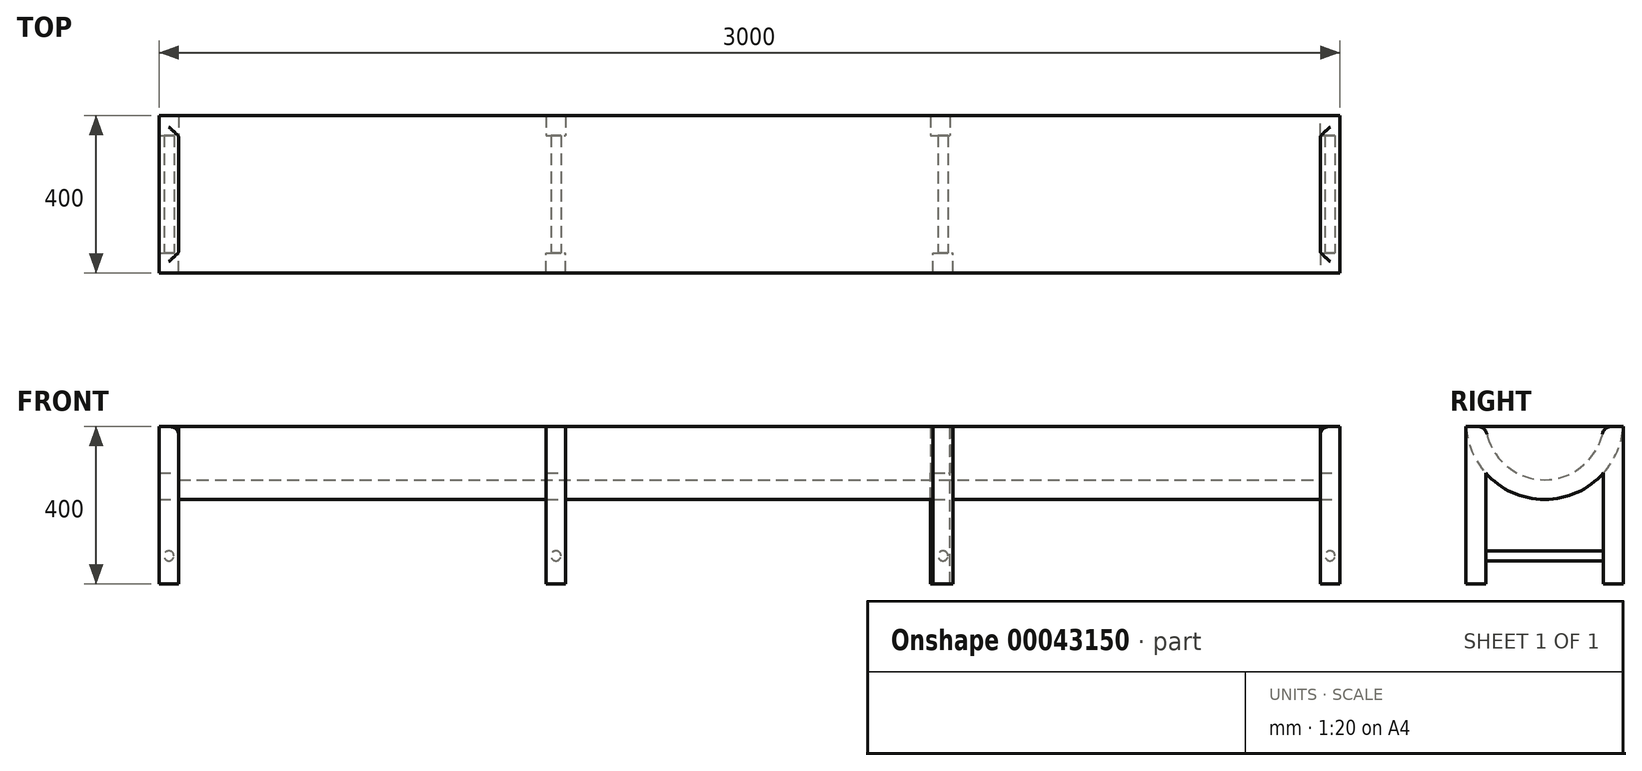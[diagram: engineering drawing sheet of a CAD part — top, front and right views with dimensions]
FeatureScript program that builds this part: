
annotation { "Feature Type Name" : "Feature", "Feature Type Description" : "" }
export const myFeature = defineFeature(function(context is Context, id is Id, definition is map)
    precondition{}
    {
        {
            var Q0;
            Q0=qCreatedBy(makeId("Right.planeOp"),FACE);
            var sketch = newSketch(context, id + "F0", { "sketchPlane" : qUnion([Q0])});
            skArc(sketch, "E0", {"start": v(-199.85, 0) * mm, "mid": v(0.15, -185.28) * mm, "end": v(200.15, 0) * mm});
            skArc(sketch, "E1.0", {"start": v(-149.66, 0) * mm, "mid": v(0.15, -135.28) * mm, "end": v(149.95, 0) * mm});
            skLineSegment(sketch, "E2", {"start": v(-199.85, 0) * mm, "end": v(-149.66, 0) * mm});
            skLineSegment(sketch, "E3", {"start": v(200.15, 0) * mm, "end": v(149.95, 0) * mm});
            skSolve(sketch);
        }
        {
            var Q0;
            Q0=makeQuery(id+"F0.imprint","IMPRINT",FACE,{"disambiguationData":[TD([[makeQuery(id+"F0.imprint","IMPRINT",EDGE,{"derivedFrom":sQuery(id+"F0.wireOp",EDGE,"E0")}),1.0]])]});
            extrude(context, id + "F1", {"entities" : qUnion([Q0]), "endBound" : BoundingType.SYMMETRIC, "oppositeDirection" : true, "depth" : 3000 * mm});
        }
        {
            var Q0;
            Q0=makeQuery(id+"F1.opExtrude","CAP_FACE",FACE,{"disambiguationData":[OSD([sQuery(id+"F0.wireOp",EDGE,"E0"),sQuery(id+"F0.wireOp",EDGE,"E1.0"),sQuery(id+"F0.wireOp",EDGE,"E2"),sQuery(id+"F0.wireOp",EDGE,"E3")])],"isStart":true});
            var sketch = newSketch(context, id + "F2", { "sketchPlane" : qUnion([Q0])});
            skLineSegment(sketch, "E4", {"start": v(-149.66, 0) * mm, "end": v(149.95, 0) * mm});
            skSolve(sketch);
        }
        {
            var Q0;
            Q0=makeQuery(id+"F2.imprint","IMPRINT",FACE,{"disambiguationData":[TD([[makeQuery(id+"F2.imprint","IMPRINT",EDGE,{"derivedFrom":sQuery(id+"F2.wireOp",EDGE,"E4")}),-1.0]])]});
            extrude(context, id + "F3", {"entities" : qUnion([Q0]), "operationType" : NewBodyOperationType.ADD, "oppositeDirection" : true, "depth" : 50 * mm});
        }
        {
            var Q0;
            Q0=makeQuery(id+"F1.opExtrude","CAP_FACE",FACE,{"disambiguationData":[OSD([sQuery(id+"F0.wireOp",EDGE,"E0"),sQuery(id+"F0.wireOp",EDGE,"E1.0"),sQuery(id+"F0.wireOp",EDGE,"E2"),sQuery(id+"F0.wireOp",EDGE,"E3")])],"isStart":false});
            var sketch = newSketch(context, id + "F4", { "sketchPlane" : qUnion([Q0])});
            skLineSegment(sketch, "E5", {"start": v(-149.95, 0) * mm, "end": v(149.66, 0) * mm});
            skSolve(sketch);
        }
        {
            var Q0;
            Q0 = qSketchRegion(id + "F4", true);
            var Q1;
            Q1=makeQuery(id+"F4.imprint","IMPRINT",FACE,{"disambiguationData":[TD([[makeQuery(id+"F4.imprint","IMPRINT",EDGE,{"derivedFrom":sQuery(id+"F4.wireOp",EDGE,"E5")}),-1.0]])]});
            extrude(context, id + "F5", {"entities" : qUnion([Q0, Q1]), "operationType" : NewBodyOperationType.ADD, "oppositeDirection" : true, "depth" : 50 * mm});
        }
        {
            var Q0;
            Q0=makeQuery(id+"F5.boolean.opBoolean","MERGE",FACE,{"derivedFrom":[makeQuery(id+"F3.boolean.opBoolean","MERGE",FACE,{"derivedFrom":[makeQuery(id+"F1.opExtrude","SWEPT_FACE",FACE,{"disambiguationData":[OSD([sQuery(id+"F0.wireOp",EDGE,"E2")])]}),makeQuery(id+"F1.opExtrude","SWEPT_FACE",FACE,{"disambiguationData":[OSD([sQuery(id+"F0.wireOp",EDGE,"E3")])]}),makeQuery(id+"F3.opExtrude","SWEPT_FACE",FACE,{"disambiguationData":[OSD([sQuery(id+"F2.wireOp",EDGE,"E4")])]})]}),makeQuery(id+"F5.opExtrude","SWEPT_FACE",FACE,{"disambiguationData":[OSD([sQuery(id+"F4.wireOp",EDGE,"E5")])]})]});
            var sketch = newSketch(context, id + "F6", { "sketchPlane" : qUnion([Q0])});
            skLineSegment(sketch, "E6.bottom", {"start": v(1450, -149.66) * mm, "end": v(1500, -149.66) * mm});
            skLineSegment(sketch, "E6.top", {"start": v(1450, -199.85) * mm, "end": v(1500, -199.85) * mm});
            skLineSegment(sketch, "E6.left", {"start": v(1450, -149.66) * mm, "end": v(1450, -199.85) * mm});
            skLineSegment(sketch, "E6.right", {"start": v(1500, -149.66) * mm, "end": v(1500, -199.85) * mm});
            skLineSegment(sketch, "E7.bottom", {"start": v(1450, 149.95) * mm, "end": v(1500, 149.95) * mm});
            skLineSegment(sketch, "E7.top", {"start": v(1450, 200.15) * mm, "end": v(1500, 200.15) * mm});
            skLineSegment(sketch, "E7.left", {"start": v(1450, 149.95) * mm, "end": v(1450, 200.15) * mm});
            skLineSegment(sketch, "E7.right", {"start": v(1500, 149.95) * mm, "end": v(1500, 200.15) * mm});
            skLineSegment(sketch, "E8.bottom", {"start": v(-1500, 200.15) * mm, "end": v(-1450, 200.15) * mm});
            skLineSegment(sketch, "E8.top", {"start": v(-1500, 149.95) * mm, "end": v(-1450, 149.95) * mm});
            skLineSegment(sketch, "E8.left", {"start": v(-1500, 200.15) * mm, "end": v(-1500, 149.95) * mm});
            skLineSegment(sketch, "E8.right", {"start": v(-1450, 200.15) * mm, "end": v(-1450, 149.95) * mm});
            skLineSegment(sketch, "E9.bottom", {"start": v(-1500, -199.85) * mm, "end": v(-1450, -199.85) * mm});
            skLineSegment(sketch, "E9.top", {"start": v(-1500, -149.66) * mm, "end": v(-1450, -149.66) * mm});
            skLineSegment(sketch, "E9.left", {"start": v(-1500, -199.85) * mm, "end": v(-1500, -149.66) * mm});
            skLineSegment(sketch, "E9.right", {"start": v(-1450, -199.85) * mm, "end": v(-1450, -149.66) * mm});
            skLineSegment(sketch, "E10.MirrorCS", {"start": v(-516.67, 200.15) * mm, "end": v(-516.67, 149.95) * mm});
            skLineSegment(sketch, "E11.MirrorCS", {"start": v(-466.67, 200.15) * mm, "end": v(-516.67, 200.15) * mm});
            skLineSegment(sketch, "E12.MirrorCS", {"start": v(-466.67, 200.15) * mm, "end": v(-466.67, 149.95) * mm});
            skLineSegment(sketch, "E13.MirrorCS", {"start": v(-466.67, 149.95) * mm, "end": v(-516.67, 149.95) * mm});
            skLineSegment(sketch, "E14.MirrorCS", {"start": v(-466.68, -149.66) * mm, "end": v(-516.68, -149.66) * mm});
            skLineSegment(sketch, "E15.MirrorCS", {"start": v(-466.68, -199.85) * mm, "end": v(-516.68, -199.85) * mm});
            skLineSegment(sketch, "E16.MirrorCS", {"start": v(-466.68, -199.85) * mm, "end": v(-466.68, -149.66) * mm});
            skLineSegment(sketch, "E17.MirrorCS", {"start": v(-516.68, -199.85) * mm, "end": v(-516.68, -149.66) * mm});
            skLineSegment(sketch, "E18.MirrorCS", {"start": v(459.8, 149.95) * mm, "end": v(509.8, 149.95) * mm});
            skLineSegment(sketch, "E19.MirrorCS", {"start": v(509.8, 200.15) * mm, "end": v(509.8, 149.95) * mm});
            skLineSegment(sketch, "E20.MirrorCS", {"start": v(459.8, 200.15) * mm, "end": v(459.8, 149.95) * mm});
            skLineSegment(sketch, "E21.MirrorCS", {"start": v(459.8, 200.15) * mm, "end": v(509.8, 200.15) * mm});
            skLineSegment(sketch, "E22.MirrorCS", {"start": v(466.65, -199.85) * mm, "end": v(466.65, -149.66) * mm});
            skLineSegment(sketch, "E23.MirrorCS", {"start": v(466.65, -149.66) * mm, "end": v(516.65, -149.66) * mm});
            skLineSegment(sketch, "E24.MirrorCS", {"start": v(516.65, -199.85) * mm, "end": v(516.65, -149.66) * mm});
            skLineSegment(sketch, "E25.MirrorCS", {"start": v(466.65, -199.85) * mm, "end": v(516.65, -199.85) * mm});
            skSolve(sketch);
        }
        {
            var Q0;
            Q0 = qSketchRegion(id + "F6", true);
            extrude(context, id + "F7", {"entities" : qUnion([Q0]), "operationType" : NewBodyOperationType.ADD, "oppositeDirection" : true, "depth" : 400 * mm});
        }
        {
            var Q0;
            Q0=makeQuery(id+"F7.opExtrude","SWEPT_FACE",FACE,{"disambiguationData":[OSD([sQuery(id+"F6.wireOp",EDGE,"E9.bottom")])]});
            var sketch = newSketch(context, id + "F8", { "sketchPlane" : qUnion([Q0])});
            skCircle(sketch, "E26", {"center": v(-1475, -328.5) * mm, "radius": 12.7 * mm});
            skCircle(sketch, "E27.1.0.0", {"center": v(-491.72, -328.5) * mm, "radius": 12.7 * mm});
            skCircle(sketch, "E27.2.0.0", {"center": v(491.57, -328.5) * mm, "radius": 12.7 * mm});
            skCircle(sketch, "E27.3.0.0", {"center": v(1474.85, -328.5) * mm, "radius": 12.7 * mm});
            skLineSegment(sketch, "E27.direction1", {"start": v(-1475, -328.5) * mm, "end": v(-491.72, -328.5) * mm, "construction": true});
            skSolve(sketch);
        }
        {
            var Q0;
            Q0 = qSketchRegion(id + "F8", true);
            extrude(context, id + "F9", {"entities" : qUnion([Q0]), "operationType" : NewBodyOperationType.ADD, "oppositeDirection" : true, "depth" : 400 * mm});
        }
        {
            var Q0;
            Q0=makeQuery(id+"F1.opExtrude","SWEPT_EDGE",EDGE,{"disambiguationData":[OSD([sQuery(id+"F0.wireOp",EDGE,"E1.0"),sQuery(id+"F0.wireOp",EDGE,"E3")])]});
            var Q1;
            Q1=makeQuery(id+"F5.opExtrude","CAP_EDGE",EDGE,{"disambiguationData":[OSD([sQuery(id+"F4.wireOp",EDGE,"E5")])],"isStart":false});
            var Q2;
            Q2=makeQuery(id+"F1.opExtrude","SWEPT_EDGE",EDGE,{"disambiguationData":[OSD([sQuery(id+"F0.wireOp",EDGE,"E1.0"),sQuery(id+"F0.wireOp",EDGE,"E2")])]});
            var Q3;
            Q3=makeQuery(id+"F3.opExtrude","CAP_EDGE",EDGE,{"disambiguationData":[OSD([sQuery(id+"F2.wireOp",EDGE,"E4")])],"isStart":false});
            fillet(context, id + "F10", {"entities" : qUnion([Q0, Q1, Q2, Q3]), "radius" : 25.4 * mm, "tangentPropagation" : true, "rho" : 0.5, "crossSection" : FilletCrossSection.CONIC, "allowEdgeOverflow" : false});
        }
    });
